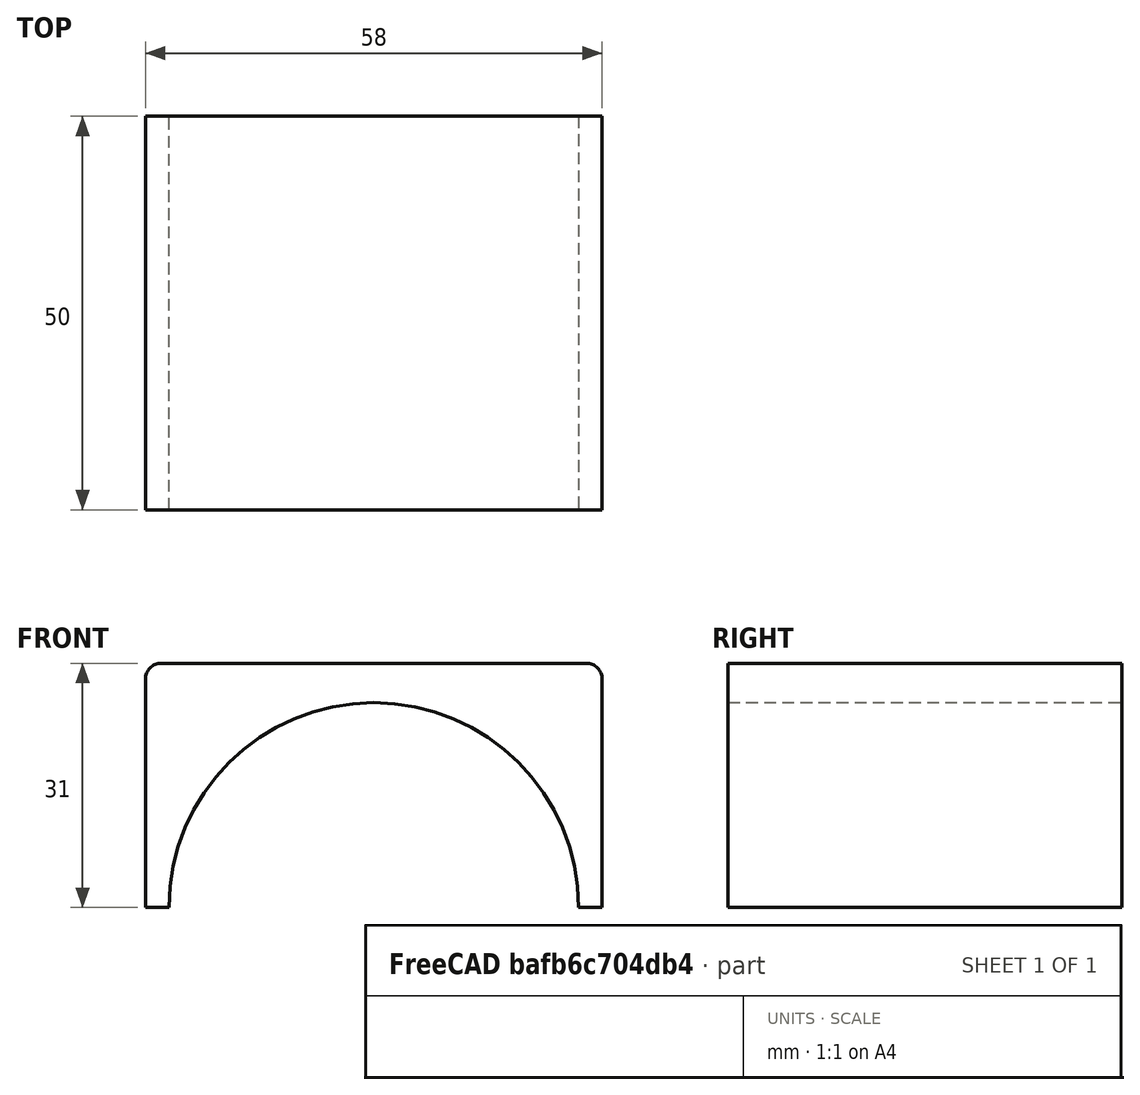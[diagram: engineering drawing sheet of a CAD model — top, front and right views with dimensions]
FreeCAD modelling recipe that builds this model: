
FCSTD DOCUMENT  (FreeCAD 0.21R33694 (Git))
Label: skalka_holder
License: All rights reserved
LicenseURL: http://en.wikipedia.org/wiki/All_rights_reserved
objects: Part::Box×1, Part::Cylinder×1, Part::Fillet×1, Part::Cut×1
note: 4 computed .brp shape members not serialized (recipe doc carries the construction recipe); baked Part::Feature solids carry a one-line shape summary decoded from their .brp

FEATURE [Part::Box] Box  label="Cube"
  AttacherType = Attacher::AttachEngine3D
  Height = 31
  Length = 58
  Placement = pos=(-29,-25,0) rot=(0,0,1;0rad)
  Width = 50
  expr: .Placement.Base.x = -Length / 2
  expr: .Placement.Base.y = -Width / 2
  expr: Height = Length / 2 + 2 mm
  expr: Length = Cylinder.Radius * 2 + 6 mm
  expr: Width = Cylinder.Height
FEATURE [Part::Cylinder] Cylinder
  Angle = 360
  AttacherType = Attacher::AttachEngine3D
  FirstAngle = 0
  Height = 50
  Placement = pos=(0,25,0) rot=(1,0,0;1.5708rad)
  Radius = 26
  SecondAngle = 0
  expr: .Placement.Base.y = Height / 2
FEATURE [Part::Fillet] Fillet
  Base = -> Box
  Edges = 2 edges r=2: [Edge2,Edge6]
FEATURE [Part::Cut] Cut  label="skalka_holder"
  Base = -> Fillet
  Tool = -> Cylinder
